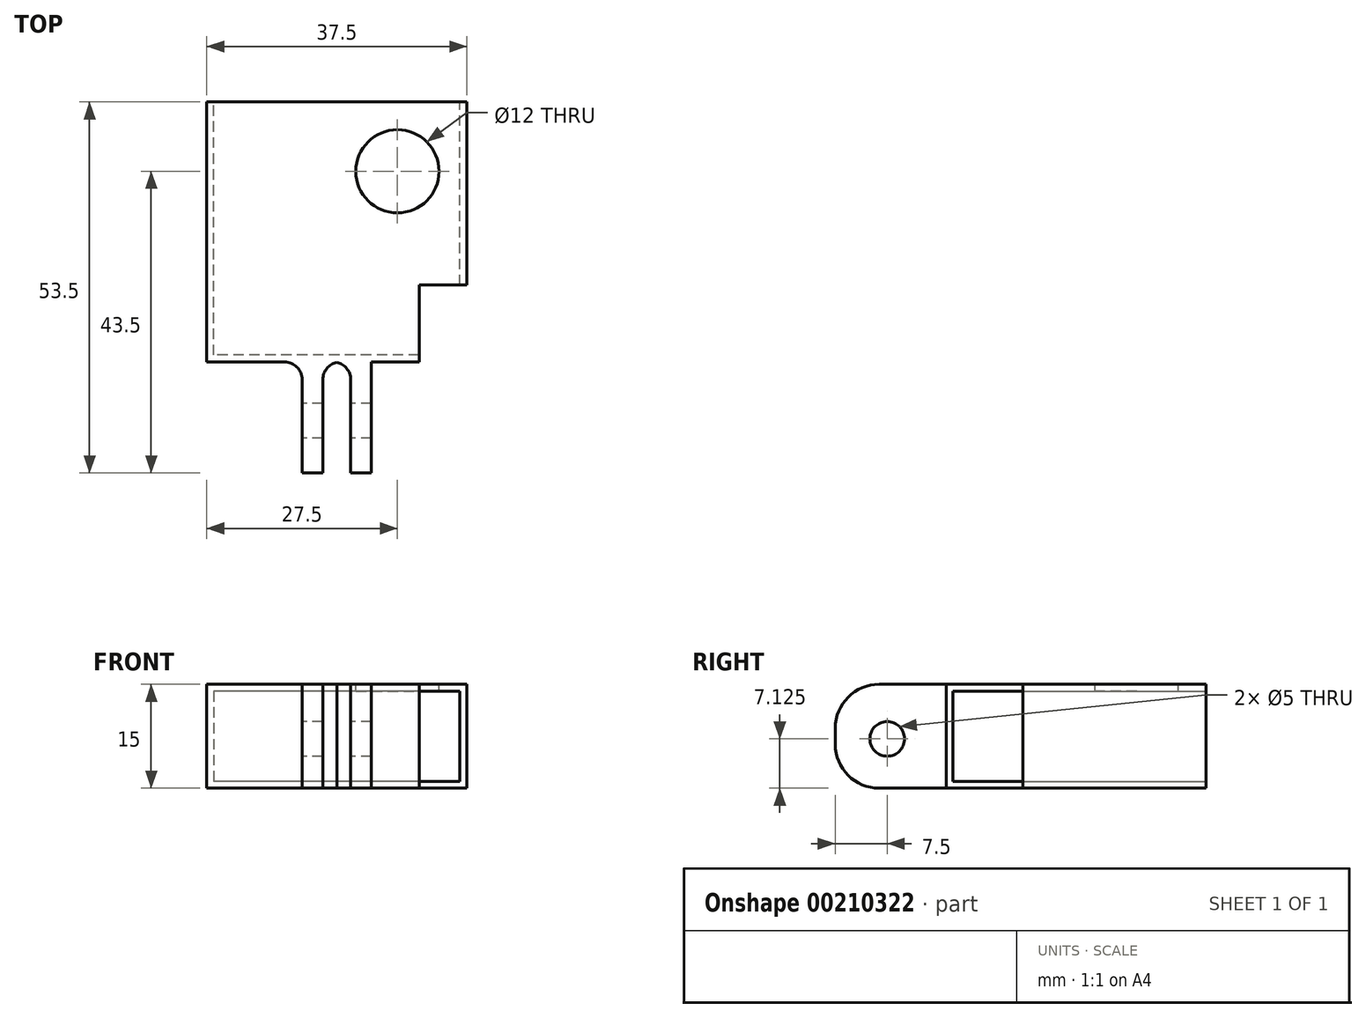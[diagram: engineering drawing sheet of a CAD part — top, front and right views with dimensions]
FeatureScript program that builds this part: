
annotation { "Feature Type Name" : "Feature", "Feature Type Description" : "" }
export const myFeature = defineFeature(function(context is Context, id is Id, definition is map)
    precondition{}
    {
        {
            var Q0;
            Q0=qCreatedBy(makeId("Top.planeOp"),FACE);
            var sketch = newSketch(context, id + "F0", { "sketchPlane" : qUnion([Q0])});
            skLineSegment(sketch, "E0.bottom", {"start": v(0, 0) * mm, "end": v(37.5, 0) * mm});
            skLineSegment(sketch, "E0.top", {"start": v(0, 37.5) * mm, "end": v(37.5, 37.5) * mm});
            skLineSegment(sketch, "E0.left", {"start": v(0, 0) * mm, "end": v(0, 37.5) * mm});
            skLineSegment(sketch, "E0.right", {"start": v(37.5, 0) * mm, "end": v(37.5, 37.5) * mm});
            skSolve(sketch);
        }
        {
            var Q0;
            Q0=makeQuery(id+"F0.imprint","IMPRINT",FACE,{"disambiguationData":[TD([[makeQuery(id+"F0.imprint","IMPRINT",EDGE,{"derivedFrom":sQuery(id+"F0.wireOp",EDGE,"E0.bottom")}),1.0]])]});
            extrude(context, id + "F1", {"entities" : qUnion([Q0]), "depth" : 15 * mm});
        }
        {
            var Q0;
            Q0=makeQuery(id+"F1.opExtrude","SWEPT_FACE",FACE,{"disambiguationData":[OSD([sQuery(id+"F0.wireOp",EDGE,"E0.top")])]});
            var sketch = newSketch(context, id + "F2", { "sketchPlane" : qUnion([Q0])});
            skLineSegment(sketch, "E1.bottom", {"start": v(-36.5, 14) * mm, "end": v(-1, 14) * mm});
            skLineSegment(sketch, "E1.top", {"start": v(-36.5, 1) * mm, "end": v(-1, 1) * mm});
            skLineSegment(sketch, "E1.left", {"start": v(-36.5, 14) * mm, "end": v(-36.5, 1) * mm});
            skLineSegment(sketch, "E1.right", {"start": v(-1, 14) * mm, "end": v(-1, 1) * mm});
            skSolve(sketch);
        }
        {
            var Q0;
            Q0 = qSketchRegion(id + "F2", true);
            extrude(context, id + "F3", {"entities" : qUnion([Q0]), "operationType" : NewBodyOperationType.REMOVE, "oppositeDirection" : true, "depth" : 36.5 * mm});
        }
        {
            var Q0;
            Q0=makeQuery(id+"F1.opExtrude","CAP_FACE",FACE,{"disambiguationData":[OSD([sQuery(id+"F0.wireOp",EDGE,"E0.bottom"),sQuery(id+"F0.wireOp",EDGE,"E0.top"),sQuery(id+"F0.wireOp",EDGE,"E0.left"),sQuery(id+"F0.wireOp",EDGE,"E0.right")])],"isStart":false});
            var sketch = newSketch(context, id + "F4", { "sketchPlane" : qUnion([Q0])});
            skCircle(sketch, "E2", {"center": v(27.5, 27.5) * mm, "radius": 6 * mm});
            skSolve(sketch);
        }
        {
            var Q0;
            Q0 = qSketchRegion(id + "F4", true);
            extrude(context, id + "F5", {"entities" : qUnion([Q0]), "operationType" : NewBodyOperationType.REMOVE, "endBound" : BoundingType.UP_TO_NEXT, "oppositeDirection" : true, "depth" : 25.4 * mm});
        }
        {
            var Q0;
            Q0=makeQuery(id+"F1.opExtrude","SWEPT_FACE",FACE,{"disambiguationData":[OSD([sQuery(id+"F0.wireOp",EDGE,"E0.bottom")])]});
            var sketch = newSketch(context, id + "F6", { "sketchPlane" : qUnion([Q0])});
            skLineSegment(sketch, "E3.bottom", {"start": v(13.75, 15) * mm, "end": v(23.75, 15) * mm});
            skLineSegment(sketch, "E3.top", {"start": v(13.75, 0) * mm, "end": v(23.75, 0) * mm});
            skLineSegment(sketch, "E3.left", {"start": v(13.75, 15) * mm, "end": v(13.75, 0) * mm});
            skLineSegment(sketch, "E3.right", {"start": v(23.75, 15) * mm, "end": v(23.75, 0) * mm});
            skSolve(sketch);
        }
        {
            var Q0;
            Q0 = qSketchRegion(id + "F6", true);
            extrude(context, id + "F7", {"entities" : qUnion([Q0]), "operationType" : NewBodyOperationType.ADD, "depth" : 16 * mm});
        }
        {
            var Q0;
            Q0=makeQuery(id+"F7.opExtrude","SWEPT_FACE",FACE,{"disambiguationData":[OSD([sQuery(id+"F6.wireOp",EDGE,"E3.left")])]});
            var sketch = newSketch(context, id + "F8", { "sketchPlane" : qUnion([Q0])});
            skCircle(sketch, "E4", {"center": v(8.5, 7.12) * mm, "radius": 2.5 * mm});
            skSolve(sketch);
        }
        {
            var Q0;
            Q0 = qSketchRegion(id + "F8", true);
            extrude(context, id + "F9", {"entities" : qUnion([Q0]), "operationType" : NewBodyOperationType.REMOVE, "oppositeDirection" : true, "depth" : 25.4 * mm});
        }
        {
            var Q0;
            Q0=makeQuery(id+"F7.opExtrude","CAP_FACE",FACE,{"disambiguationData":[OSD([sQuery(id+"F6.wireOp",EDGE,"E3.bottom"),sQuery(id+"F6.wireOp",EDGE,"E3.top"),sQuery(id+"F6.wireOp",EDGE,"E3.left"),sQuery(id+"F6.wireOp",EDGE,"E3.right")])],"isStart":false});
            var sketch = newSketch(context, id + "F10", { "sketchPlane" : qUnion([Q0])});
            skLineSegment(sketch, "E5.bottom", {"start": v(16.75, 15) * mm, "end": v(20.75, 15) * mm});
            skLineSegment(sketch, "E5.top", {"start": v(16.75, 0) * mm, "end": v(20.75, 0) * mm});
            skLineSegment(sketch, "E5.left", {"start": v(16.75, 15) * mm, "end": v(16.75, 0) * mm});
            skLineSegment(sketch, "E5.right", {"start": v(20.75, 15) * mm, "end": v(20.75, 0) * mm});
            skSolve(sketch);
        }
        {
            var Q0;
            Q0 = qSketchRegion(id + "F10", true);
            extrude(context, id + "F11", {"entities" : qUnion([Q0]), "operationType" : NewBodyOperationType.REMOVE, "oppositeDirection" : true, "depth" : 16 * mm});
        }
        {
            var Q0;
            {var subQ0=sQuery(id+"F6.wireOp",EDGE,"E3.left");var subQ1=sQuery(id+"F6.wireOp",EDGE,"E3.bottom");Q0=makeQuery(id+"F11.boolean.opBoolean","SPLIT",EDGE,{"disambiguationData":[TD([makeQuery(id+"F7.opExtrude","SWEPT_FACE",FACE,{"disambiguationData":[OSD([subQ0])]})])],"derivedFrom":makeQuery(id+"F7.opExtrude","CAP_EDGE",EDGE,{"disambiguationData":[OSD([subQ1])],"isStart":false})});}
            var Q1;
            {var subQ0=sQuery(id+"F6.wireOp",EDGE,"E3.right");var subQ1=sQuery(id+"F6.wireOp",EDGE,"E3.bottom");Q1=makeQuery(id+"F11.boolean.opBoolean","SPLIT",EDGE,{"disambiguationData":[TD([makeQuery(id+"F7.opExtrude","SWEPT_FACE",FACE,{"disambiguationData":[OSD([subQ0])]})])],"derivedFrom":makeQuery(id+"F7.opExtrude","CAP_EDGE",EDGE,{"disambiguationData":[OSD([subQ1])],"isStart":false})});}
            var Q2;
            {var subQ0=sQuery(id+"F6.wireOp",EDGE,"E3.right");var subQ1=sQuery(id+"F6.wireOp",EDGE,"E3.top");Q2=makeQuery(id+"F11.boolean.opBoolean","SPLIT",EDGE,{"disambiguationData":[TD([makeQuery(id+"F7.opExtrude","SWEPT_FACE",FACE,{"disambiguationData":[OSD([subQ0])]})])],"derivedFrom":makeQuery(id+"F7.opExtrude","CAP_EDGE",EDGE,{"disambiguationData":[OSD([subQ1])],"isStart":false})});}
            var Q3;
            {var subQ0=sQuery(id+"F6.wireOp",EDGE,"E3.left");var subQ1=sQuery(id+"F6.wireOp",EDGE,"E3.top");Q3=makeQuery(id+"F11.boolean.opBoolean","SPLIT",EDGE,{"disambiguationData":[TD([makeQuery(id+"F7.opExtrude","SWEPT_FACE",FACE,{"disambiguationData":[OSD([subQ0])]})])],"derivedFrom":makeQuery(id+"F7.opExtrude","CAP_EDGE",EDGE,{"disambiguationData":[OSD([subQ1])],"isStart":false})});}
            fillet(context, id + "F12", {"entities" : qUnion([Q0, Q1, Q2, Q3]), "radius" : 6.35 * mm, "tangentPropagation" : true, "allowEdgeOverflow" : false});
        }
        {
            var Q0;
            Q0=makeQuery(id+"F7.boolean.opBoolean","MERGE",FACE,{"derivedFrom":[makeQuery(id+"F1.opExtrude","CAP_FACE",FACE,{"disambiguationData":[OSD([sQuery(id+"F0.wireOp",EDGE,"E0.bottom"),sQuery(id+"F0.wireOp",EDGE,"E0.top"),sQuery(id+"F0.wireOp",EDGE,"E0.left"),sQuery(id+"F0.wireOp",EDGE,"E0.right")])],"isStart":false}),makeQuery(id+"F7.opExtrude","SWEPT_FACE",FACE,{"disambiguationData":[OSD([sQuery(id+"F6.wireOp",EDGE,"E3.bottom")])]})]});
            var sketch = newSketch(context, id + "F13", { "sketchPlane" : qUnion([Q0])});
            skPoint(sketch, "E6.oppositeSnap0", {"position": v(30.62, 0) * mm});
            skLineSegment(sketch, "E6.bottom", {"start": v(37.5, 0) * mm, "end": v(30.62, 0) * mm});
            skLineSegment(sketch, "E6.top", {"start": v(37.5, 11.09) * mm, "end": v(30.62, 11.09) * mm});
            skLineSegment(sketch, "E6.left", {"start": v(37.5, 0) * mm, "end": v(37.5, 11.09) * mm});
            skLineSegment(sketch, "E6.right", {"start": v(30.62, 0) * mm, "end": v(30.62, 11.09) * mm});
            skSolve(sketch);
        }
        {
            var Q0;
            Q0=makeQuery(id+"F13.imprint","IMPRINT",FACE,{"disambiguationData":[TD([[makeQuery(id+"F13.imprint","IMPRINT",EDGE,{"derivedFrom":sQuery(id+"F13.wireOp",EDGE,"E6.bottom")}),1.0]])]});
            extrude(context, id + "F14", {"entities" : qUnion([Q0]), "operationType" : NewBodyOperationType.REMOVE, "oppositeDirection" : true, "depth" : 25.4 * mm});
        }
        {
            var Q0;
            Q0=makeQuery(id+"F7.opExtrude","CAP_EDGE",EDGE,{"disambiguationData":[OSD([sQuery(id+"F6.wireOp",EDGE,"E3.right")])],"isStart":true});
            var Q1;
            Q1=makeQuery(id+"F11.boolean.opBoolean","COPY",EDGE,{"derivedFrom":makeQuery(id+"F11.opExtrude","CAP_EDGE",EDGE,{"disambiguationData":[OSD([sQuery(id+"F10.wireOp",EDGE,"E5.right")])],"isStart":false})});
            var Q2;
            Q2=makeQuery(id+"F7.opExtrude","CAP_EDGE",EDGE,{"disambiguationData":[OSD([sQuery(id+"F6.wireOp",EDGE,"E3.left")])],"isStart":true});
            var Q3;
            Q3=makeQuery(id+"F11.boolean.opBoolean","COPY",EDGE,{"derivedFrom":makeQuery(id+"F11.opExtrude","CAP_EDGE",EDGE,{"disambiguationData":[OSD([sQuery(id+"F10.wireOp",EDGE,"E5.left")])],"isStart":false})});
            fillet(context, id + "F15", {"entities" : qUnion([Q0, Q1, Q2, Q3]), "radius" : 2.54 * mm, "tangentPropagation" : true, "allowEdgeOverflow" : false});
        }
    });
